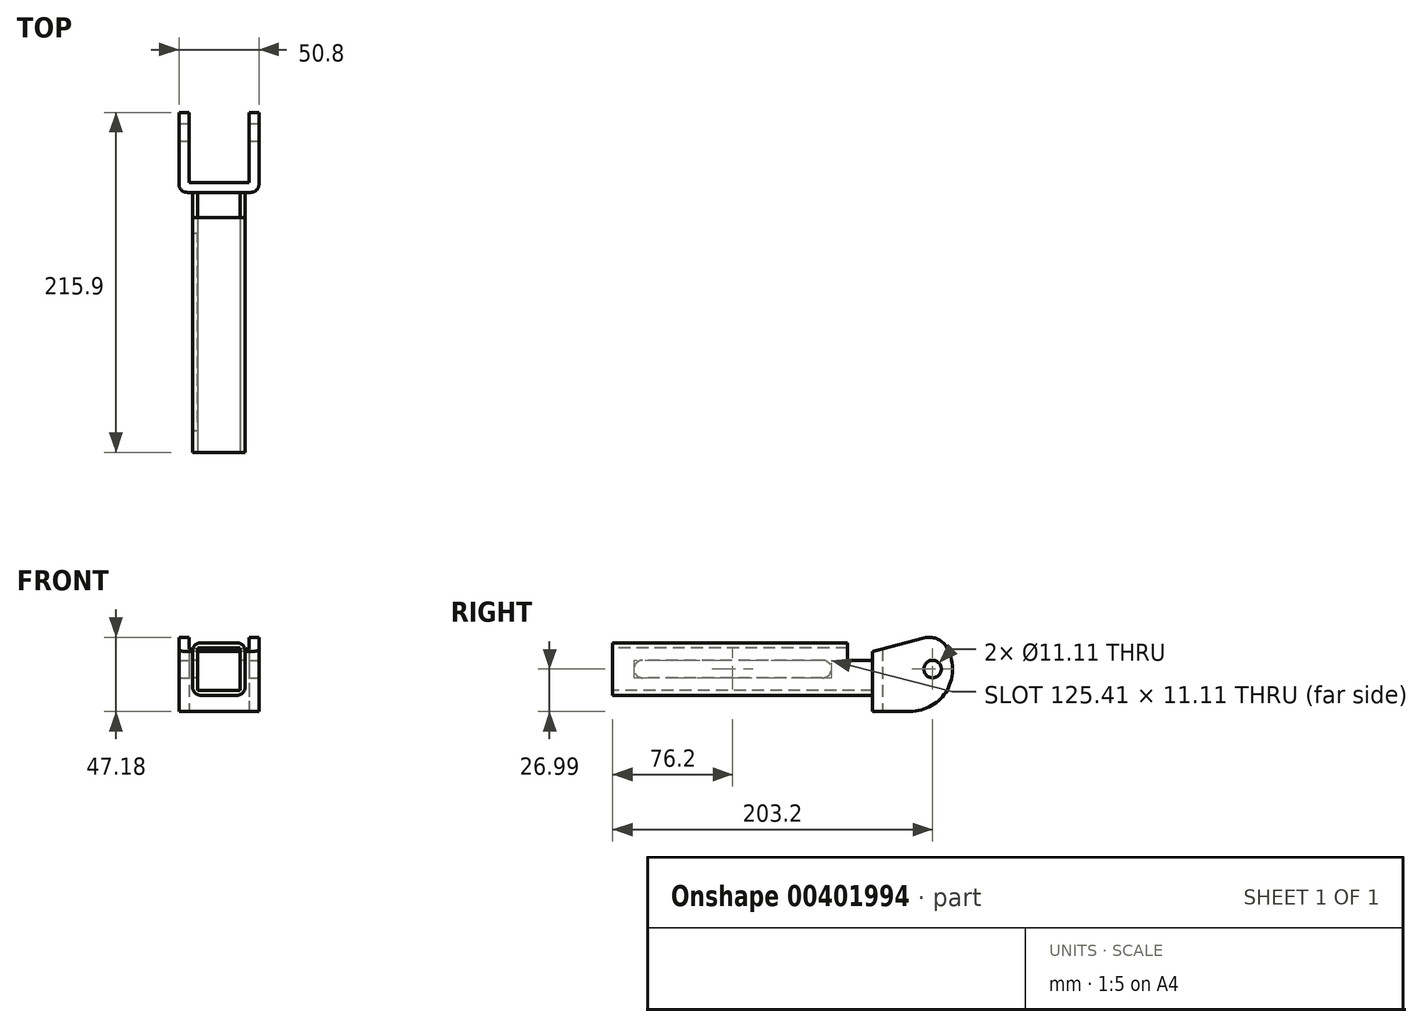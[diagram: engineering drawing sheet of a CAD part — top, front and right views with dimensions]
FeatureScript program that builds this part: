
annotation { "Feature Type Name" : "Feature", "Feature Type Description" : "" }
export const myFeature = defineFeature(function(context is Context, id is Id, definition is map)
    precondition{}
    {
        {
            var Q0;
            Q0=qCreatedBy(makeId("Front.planeOp"),FACE);
            var sketch = newSketch(context, id + "F0", { "sketchPlane" : qUnion([Q0])});
            skLineSegment(sketch, "E0.bottom", {"start": v(13.5, 13.5) * mm, "end": v(-13.5, 13.5) * mm});
            skLineSegment(sketch, "E0.top", {"start": v(13.5, -13.5) * mm, "end": v(-13.5, -13.5) * mm});
            skLineSegment(sketch, "E0.left", {"start": v(13.5, 13.5) * mm, "end": v(13.5, -13.5) * mm});
            skLineSegment(sketch, "E0.right", {"start": v(-13.5, 13.5) * mm, "end": v(-13.5, -13.5) * mm});
            skPoint(sketch, "E0.middle", {"position": v(0, 0) * mm});
            skLineSegment(sketch, "E1.bottom", {"start": v(16.67, 16.68) * mm, "end": v(-16.67, 16.68) * mm});
            skLineSegment(sketch, "E1.top", {"start": v(16.67, -16.68) * mm, "end": v(-16.67, -16.68) * mm});
            skLineSegment(sketch, "E1.left", {"start": v(16.67, 16.68) * mm, "end": v(16.67, -16.68) * mm});
            skLineSegment(sketch, "E1.right", {"start": v(-16.67, 16.68) * mm, "end": v(-16.67, -16.68) * mm});
            skSolve(sketch);
        }
        {
            var Q0;
            Q0=makeQuery(id+"F0.imprint","IMPRINT",FACE,{"disambiguationData":[TD([[makeQuery(id+"F0.imprint","IMPRINT",EDGE,{"derivedFrom":sQuery(id+"F0.wireOp",EDGE,"E0.bottom")}),-1.0]])]});
            extrude(context, id + "F1", {"entities" : qUnion([Q0]), "oppositeDirection" : true, "depth" : 165.1 * mm});
        }
        {
            var Q0;
            Q0=makeQuery(id+"F1.opExtrude","SWEPT_FACE",FACE,{"disambiguationData":[OSD([sQuery(id+"F0.wireOp",EDGE,"E1.right")])]});
            var sketch = newSketch(context, id + "F2", { "sketchPlane" : qUnion([Q0])});
            skLineSegment(sketch, "E2.bottom", {"start": v(-165.1, 16.68) * mm, "end": v(-149.23, 16.68) * mm});
            skLineSegment(sketch, "E2.top", {"start": v(-165.1, 5.56) * mm, "end": v(-149.23, 5.56) * mm});
            skLineSegment(sketch, "E2.left", {"start": v(-165.1, 16.68) * mm, "end": v(-165.1, 5.56) * mm});
            skLineSegment(sketch, "E2.right", {"start": v(-149.23, 16.68) * mm, "end": v(-149.23, 5.56) * mm});
            skSolve(sketch);
        }
        {
            var Q0;
            Q0=makeQuery(id+"F2.imprint","IMPRINT",FACE,{"disambiguationData":[TD([[makeQuery(id+"F2.imprint","IMPRINT",EDGE,{"derivedFrom":sQuery(id+"F2.wireOp",EDGE,"E2.bottom")}),-1.0]])]});
            extrude(context, id + "F3", {"entities" : qUnion([Q0]), "operationType" : NewBodyOperationType.REMOVE, "endBound" : BoundingType.THROUGH_ALL, "oppositeDirection" : true, "depth" : 25.4 * mm});
        }
        {
            var Q0;
            Q0=qCreatedBy(makeId("Top.planeOp"),FACE);
            var sketch = newSketch(context, id + "F4", { "sketchPlane" : qUnion([Q0])});
            skLineSegment(sketch, "E3.bottom", {"start": v(25.4, 165.1) * mm, "end": v(-25.4, 165.1) * mm});
            skLineSegment(sketch, "E3.left", {"start": v(25.4, 165.1) * mm, "end": v(25.4, 215.9) * mm});
            skLineSegment(sketch, "E3.right", {"start": v(-25.4, 165.1) * mm, "end": v(-25.4, 215.9) * mm});
            skLineSegment(sketch, "E4.bottom", {"start": v(19.05, 171.45) * mm, "end": v(-19.05, 171.45) * mm});
            skLineSegment(sketch, "E4.left", {"start": v(19.05, 171.45) * mm, "end": v(19.05, 215.9) * mm});
            skLineSegment(sketch, "E4.right", {"start": v(-19.05, 171.45) * mm, "end": v(-19.05, 215.9) * mm});
            skPoint(sketch, "E4.middle", {"position": v(0, 193.68) * mm});
            skLineSegment(sketch, "E5", {"start": v(19.05, 215.9) * mm, "end": v(25.4, 215.9) * mm});
            skLineSegment(sketch, "E6", {"start": v(-19.05, 215.9) * mm, "end": v(-25.4, 215.9) * mm});
            skSolve(sketch);
        }
        {
            var Q0;
            Q0=makeQuery(id+"F4.imprint","IMPRINT",FACE,{"disambiguationData":[TD([[makeQuery(id+"F4.imprint","IMPRINT",EDGE,{"derivedFrom":sQuery(id+"F4.wireOp",EDGE,"E3.bottom")}),-1.0]])]});
            extrude(context, id + "F5", {"entities" : qUnion([Q0]), "operationType" : NewBodyOperationType.ADD, "depth" : 53.97 * mm, "symmetric" : true});
        }
        {
            var Q0;
            Q0=makeQuery(id+"F5.opExtrude","SWEPT_FACE",FACE,{"disambiguationData":[OSD([sQuery(id+"F4.wireOp",EDGE,"E3.right")])]});
            var sketch = newSketch(context, id + "F6", { "sketchPlane" : qUnion([Q0])});
            skArc(sketch, "E7", {"start": v(-205, 21.67) * mm, "mid": v(-206.52, -20.45) * mm, "end": v(-165.1, -12.7) * mm});
            skPoint(sketch, "E8", {"position": v(-165.1, 11.11) * mm});
            skLineSegment(sketch, "E9", {"start": v(-165.1, 11.11) * mm, "end": v(-205, 21.67) * mm});
            skLineSegment(sketch, "E10", {"start": v(-165.1, 11.11) * mm, "end": v(-165.1, -12.7) * mm});
            skSolve(sketch);
        }
        {
            var Q0;
            {var subQ3=sQuery(id+"F6.wireOp",EDGE,"E9");Q0=makeQuery(id+"F6.imprint","IMPRINT",FACE,{"disambiguationData":[TD([[makeQuery(id+"F6.imprint","IMPRINT",EDGE,{"derivedFrom":subQ3}),-1.0]])]});}
            var Q1;
            {var subQ0=sQuery(id+"F6.wireOp",EDGE,"E7");var subQ1=sQuery(id+"F4.wireOp",EDGE,"E3.right");var subQ4=makeQuery(id+"F5.opExtrude","CAP_EDGE",EDGE,{"disambiguationData":[OSD([subQ1])],"isStart":true});var subQ5=makeQuery(id+"F6.imprint","INTERSECT",VERTEX,{"derivedFrom":[subQ4,subQ0]});Q1=makeQuery(id+"F6.imprint","IMPRINT",FACE,{"disambiguationData":[TD([[makeQuery(id+"F6.imprint","IMPRINT",EDGE,{"disambiguationData":[TD([[subQ5,1.0]])],"derivedFrom":subQ0}),-1.0]])]});}
            extrude(context, id + "F7", {"entities" : qUnion([Q0, Q1]), "operationType" : NewBodyOperationType.REMOVE, "endBound" : BoundingType.THROUGH_ALL, "oppositeDirection" : true, "depth" : 25.4 * mm});
        }
        {
            var Q0;
            Q0=makeQuery(id+"F5.opExtrude","SWEPT_EDGE",EDGE,{"disambiguationData":[OSD([sQuery(id+"F4.wireOp",EDGE,"E3.bottom"),sQuery(id+"F4.wireOp",EDGE,"E3.right")])]});
            var Q1;
            Q1=makeQuery(id+"F5.opExtrude","SWEPT_EDGE",EDGE,{"disambiguationData":[OSD([sQuery(id+"F4.wireOp",EDGE,"E3.bottom"),sQuery(id+"F4.wireOp",EDGE,"E3.left")])]});
            var Q2;
            Q2=makeQuery(id+"F1.opExtrude","SWEPT_EDGE",EDGE,{"disambiguationData":[OSD([sQuery(id+"F0.wireOp",EDGE,"E1.bottom"),sQuery(id+"F0.wireOp",EDGE,"E1.right")])]});
            var Q3;
            Q3=makeQuery(id+"F1.opExtrude","SWEPT_EDGE",EDGE,{"disambiguationData":[OSD([sQuery(id+"F0.wireOp",EDGE,"E1.bottom"),sQuery(id+"F0.wireOp",EDGE,"E1.left")])]});
            var Q4;
            Q4=makeQuery(id+"F1.opExtrude","SWEPT_EDGE",EDGE,{"disambiguationData":[OSD([sQuery(id+"F0.wireOp",EDGE,"E1.top"),sQuery(id+"F0.wireOp",EDGE,"E1.right")])]});
            var Q5;
            Q5=makeQuery(id+"F1.opExtrude","SWEPT_EDGE",EDGE,{"disambiguationData":[OSD([sQuery(id+"F0.wireOp",EDGE,"E1.top"),sQuery(id+"F0.wireOp",EDGE,"E1.left")])]});
            fillet(context, id + "F8", {"entities" : qUnion([Q0, Q1, Q2, Q3, Q4, Q5]), "radius" : 5.08 * mm, "tangentPropagation" : true, "allowEdgeOverflow" : false});
        }
        {
            var Q0;
            {var subQ0=sQuery(id+"F6.wireOp",EDGE,"E7");var subQ3=sQuery(id+"F6.wireOp",EDGE,"E9");Q0=makeQuery(id+"F7.boolean.opBoolean","COPY",EDGE,{"disambiguationData":[TD([makeQuery(id+"F5.opExtrude","SWEPT_FACE",FACE,{"disambiguationData":[OSD([sQuery(id+"F4.wireOp",EDGE,"E3.left")])]})])],"derivedFrom":makeQuery(id+"F7.opExtrude","SWEPT_EDGE",EDGE,{"disambiguationData":[OSD([subQ0,subQ3])]})});}
            var Q1;
            {var subQ0=sQuery(id+"F6.wireOp",EDGE,"E7");var subQ1=sQuery(id+"F4.wireOp",EDGE,"E3.right");var subQ3=sQuery(id+"F6.wireOp",EDGE,"E9");Q1=makeQuery(id+"F7.boolean.opBoolean","COPY",EDGE,{"disambiguationData":[TD([makeQuery(id+"F5.opExtrude","SWEPT_FACE",FACE,{"disambiguationData":[OSD([subQ1])]})])],"derivedFrom":makeQuery(id+"F7.opExtrude","SWEPT_EDGE",EDGE,{"disambiguationData":[OSD([subQ0,subQ3])]})});}
            fillet(context, id + "F9", {"entities" : qUnion([Q0, Q1]), "radius" : 12.7 * mm, "tangentPropagation" : true, "allowEdgeOverflow" : false});
        }
        {
            var Q0;
            Q0=makeQuery(id+"F5.opExtrude","SWEPT_FACE",FACE,{"disambiguationData":[OSD([sQuery(id+"F4.wireOp",EDGE,"E3.right")])]});
            var sketch = newSketch(context, id + "F10", { "sketchPlane" : qUnion([Q0])});
            skPoint(sketch, "E11", {"position": v(-203.2, 0) * mm});
            skSolve(sketch);
        }
        {
            var Q0;
            Q0=sQuery(id+"F10.wireOp",VERTEX,"E11");
            var Q1;
            Q1=makeQuery(id+"F1.opExtrude","SWEPT_BODY",BODY,{"disambiguationData":[OSD([sQuery(id+"F0.wireOp",EDGE,"E0.bottom"),sQuery(id+"F0.wireOp",EDGE,"E0.top"),sQuery(id+"F0.wireOp",EDGE,"E0.left"),sQuery(id+"F0.wireOp",EDGE,"E0.right"),sQuery(id+"F0.wireOp",EDGE,"E1.bottom"),sQuery(id+"F0.wireOp",EDGE,"E1.top"),sQuery(id+"F0.wireOp",EDGE,"E1.left"),sQuery(id+"F0.wireOp",EDGE,"E1.right")])]});
            hole(context, id + "F11", {"style" : HoleStyle.SIMPLE, "endStyle" : HoleEndStyle.THROUGH, "holeDiameter" : 11.1 * mm, "isTappedThrough" : true, "tappedDepth" : 12.7 * mm, "tapClearance" : 3, "locations" : qUnion([Q0]), "scope" : qUnion([Q1])});
        }
        {
            var Q0;
            Q0=makeQuery(id+"F1.opExtrude","SWEPT_FACE",FACE,{"disambiguationData":[OSD([sQuery(id+"F0.wireOp",EDGE,"E1.right")])]});
            var sketch = newSketch(context, id + "F12", { "sketchPlane" : qUnion([Q0])});
            skArc(sketch, "E12", {"start": v(-133.35, 5.56) * mm, "mid": v(-138.9, 0) * mm, "end": v(-133.35, -5.56) * mm});
            skArc(sketch, "E13", {"start": v(-19.05, -5.56) * mm, "mid": v(-13.5, 0) * mm, "end": v(-19.05, 5.56) * mm});
            skLineSegment(sketch, "E14", {"start": v(-133.35, 5.56) * mm, "end": v(-19.05, 5.56) * mm});
            skLineSegment(sketch, "E15", {"start": v(-133.35, -5.56) * mm, "end": v(-19.05, -5.56) * mm});
            skSolve(sketch);
        }
        {
            var Q0;
            Q0=makeQuery(id+"F12.imprint","IMPRINT",FACE,{"disambiguationData":[TD([[makeQuery(id+"F12.imprint","IMPRINT",EDGE,{"derivedFrom":sQuery(id+"F12.wireOp",EDGE,"E12")}),1.0]])]});
            extrude(context, id + "F13", {"entities" : qUnion([Q0]), "operationType" : NewBodyOperationType.REMOVE, "endBound" : BoundingType.UP_TO_NEXT, "oppositeDirection" : true, "depth" : 25.4 * mm});
        }
    });
